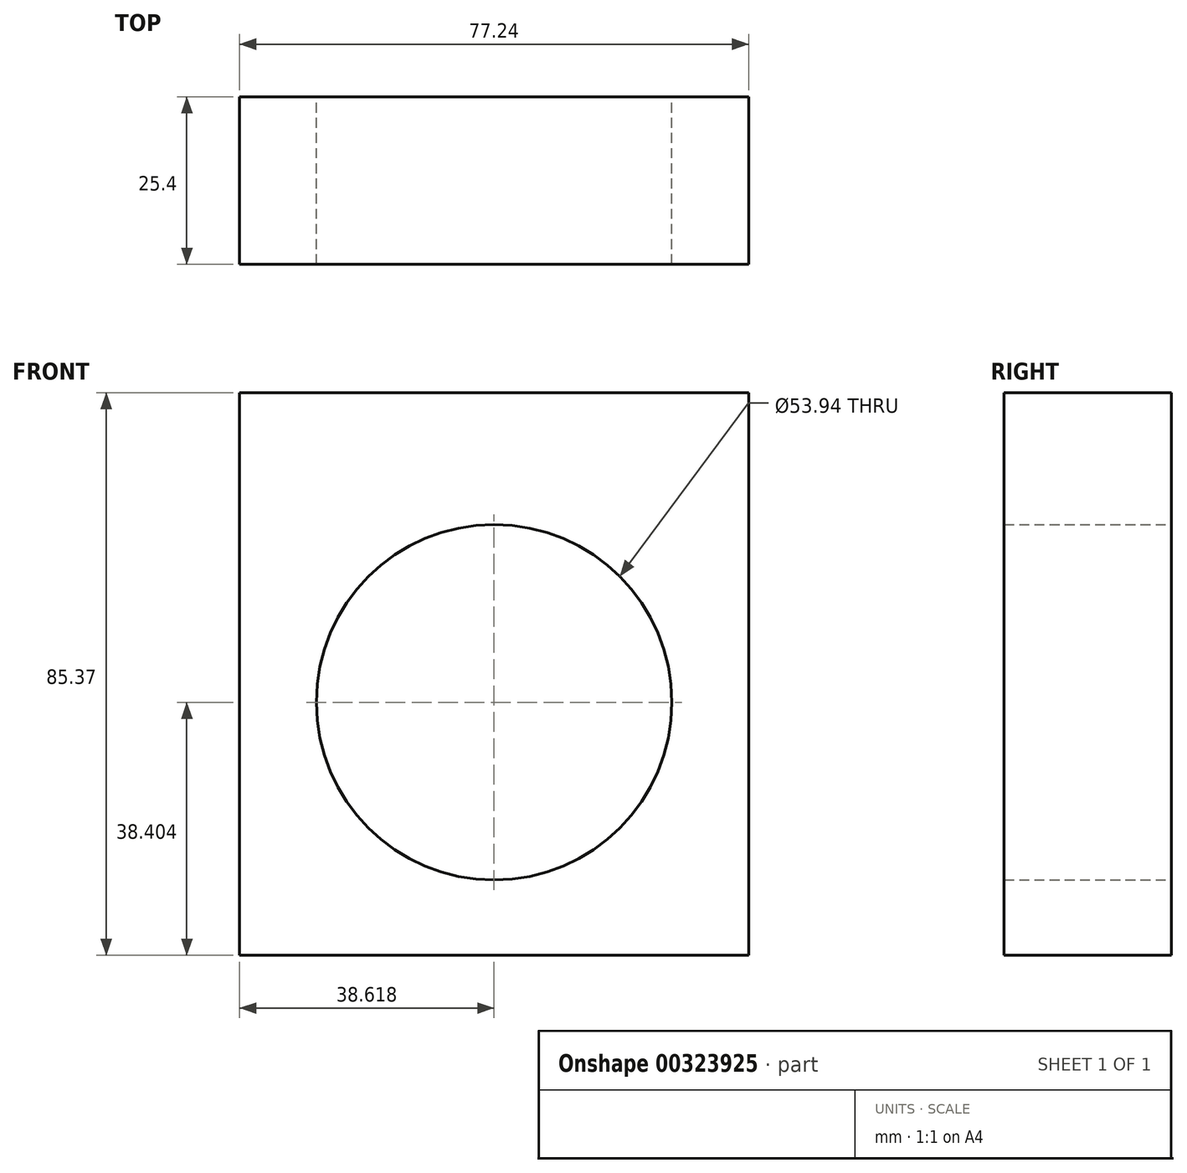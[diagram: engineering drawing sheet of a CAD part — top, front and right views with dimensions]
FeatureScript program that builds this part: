
annotation { "Feature Type Name" : "Feature", "Feature Type Description" : "" }
export const myFeature = defineFeature(function(context is Context, id is Id, definition is map)
    precondition{}
    {
        {
            var Q0;
            Q0=qCreatedBy(makeId("Front.planeOp"),FACE);
            var sketch = newSketch(context, id + "F0", { "sketchPlane" : qUnion([Q0])});
            skLineSegment(sketch, "E0.bottom", {"start": v(0, 0) * mm, "end": v(77.24, 0) * mm});
            skLineSegment(sketch, "E0.top", {"start": v(0, 85.37) * mm, "end": v(77.24, 85.37) * mm});
            skLineSegment(sketch, "E0.left", {"start": v(0, 0) * mm, "end": v(0, 85.37) * mm});
            skLineSegment(sketch, "E0.right", {"start": v(77.24, 0) * mm, "end": v(77.24, 85.37) * mm});
            skSolve(sketch);
        }
        {
            var Q0;
            Q0 = qSketchRegion(id + "F0", true);
            extrude(context, id + "F1", {"entities" : qUnion([Q0]), "depth" : 25.4 * mm});
        }
        {
            var Q0;
            Q0=makeQuery(id+"F1.opExtrude","CAP_FACE",FACE,{"disambiguationData":[OSD([sQuery(id+"F0.wireOp",EDGE,"E0.bottom"),sQuery(id+"F0.wireOp",EDGE,"E0.top"),sQuery(id+"F0.wireOp",EDGE,"E0.left"),sQuery(id+"F0.wireOp",EDGE,"E0.right")])],"isStart":true});
            var sketch = newSketch(context, id + "F2", { "sketchPlane" : qUnion([Q0])});
            skCircle(sketch, "E1", {"center": v(-38.62, 38.4) * mm, "radius": 26.97 * mm});
            skPoint(sketch, "E1.centerSnap0", {"position": v(-38.62, 0) * mm});
            skSolve(sketch);
        }
        {
            var Q0;
            Q0 = qSketchRegion(id + "F2", true);
            extrude(context, id + "F3", {"entities" : qUnion([Q0]), "operationType" : NewBodyOperationType.REMOVE, "oppositeDirection" : true, "depth" : 25.4 * mm});
        }
    });
